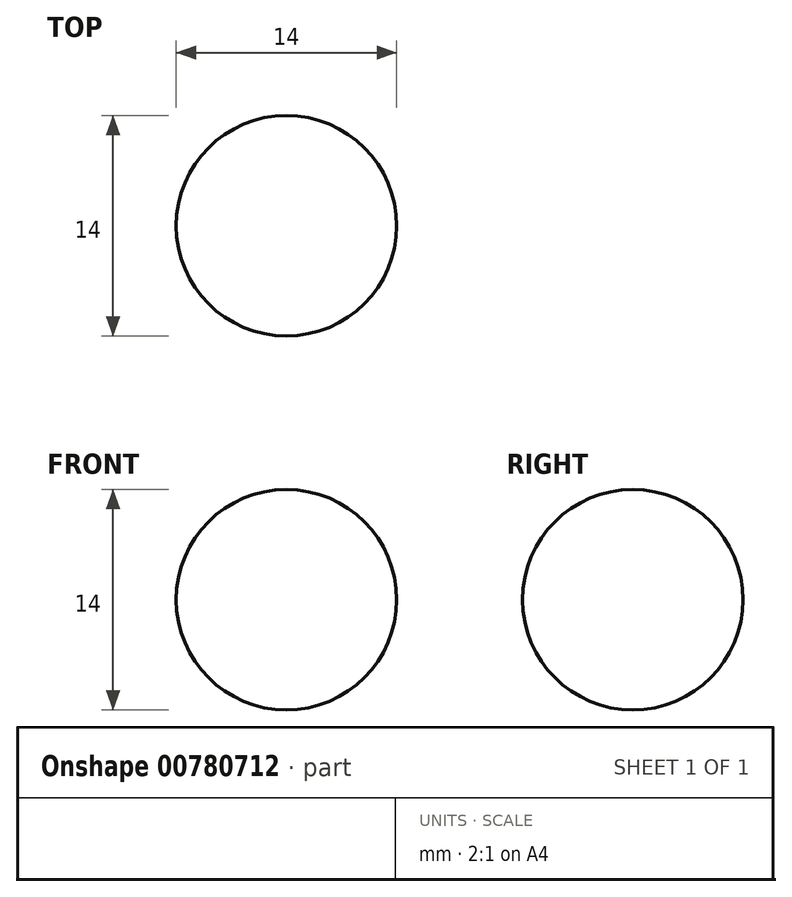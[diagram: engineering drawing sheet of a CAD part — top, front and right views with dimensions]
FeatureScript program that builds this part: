
annotation { "Feature Type Name" : "Feature", "Feature Type Description" : "" }
export const myFeature = defineFeature(function(context is Context, id is Id, definition is map)
    precondition{}
    {
        {
            var Q0;
            Q0=qCreatedBy(makeId("Front.planeOp"),FACE);
            var sketch = newSketch(context, id + "F0", { "sketchPlane" : qUnion([Q0])});
            skLineSegment(sketch, "E0", {"start": v(0, 0) * mm, "end": v(0, 7) * mm});
            skLineSegment(sketch, "E1", {"start": v(0, 0) * mm, "end": v(0, -7) * mm});
            skArc(sketch, "E2", {"start": v(0, -7) * mm, "mid": v(7, 0) * mm, "end": v(0, 7) * mm});
            skSolve(sketch);
        }
        {
            var Q0;
            Q0=qSketchRegion(id+"F0",true);
            var Q1;
            Q1=sQuery(id+"F0.wireOp",EDGE,"E0");
            revolve(context, id + "F1", {"surfaceOperationType" : NewSurfaceOperationType.NEW, "entities" : qUnion([Q0]), "axis" : qUnion([Q1]), "revolveType" : RevolveType.FULL});
        }
    });
